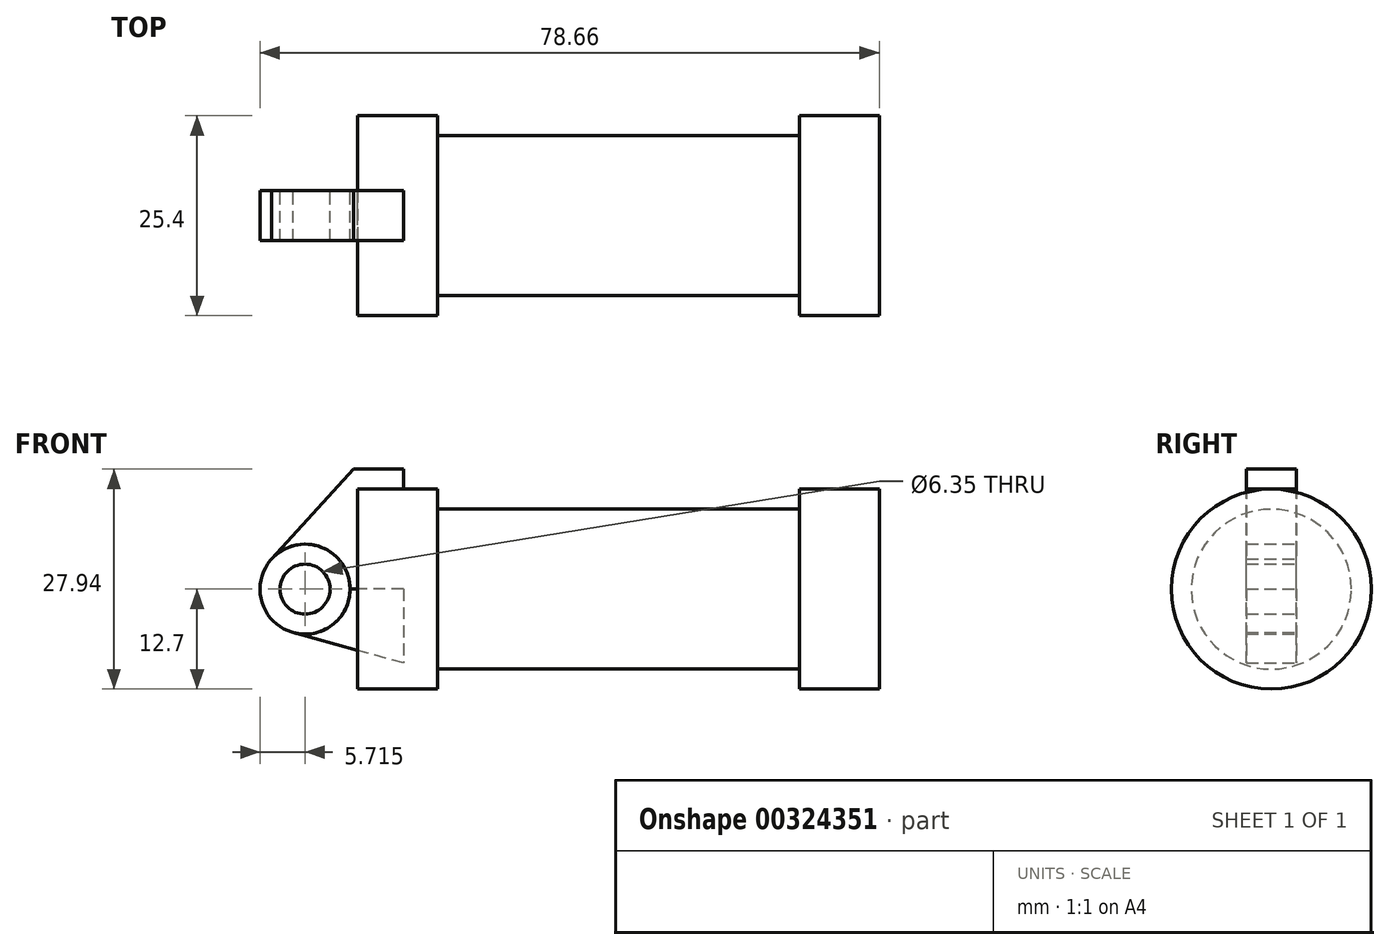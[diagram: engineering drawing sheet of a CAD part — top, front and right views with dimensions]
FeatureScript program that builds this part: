
annotation { "Feature Type Name" : "Feature", "Feature Type Description" : "" }
export const myFeature = defineFeature(function(context is Context, id is Id, definition is map)
    precondition{}
    {
        {
            var Q0;
            Q0=qCreatedBy(makeId("Front.planeOp"),FACE);
            var sketch = newSketch(context, id + "F0", { "sketchPlane" : qUnion([Q0])});
            skLineSegment(sketch, "E0", {"start": v(0, 0) * mm, "end": v(0, 12.7) * mm});
            skLineSegment(sketch, "E1", {"start": v(0, 12.7) * mm, "end": v(10.16, 12.7) * mm});
            skLineSegment(sketch, "E2", {"start": v(10.16, 12.7) * mm, "end": v(10.16, 10.16) * mm});
            skLineSegment(sketch, "E3", {"start": v(10.16, 10.16) * mm, "end": v(56.13, 10.16) * mm});
            skLineSegment(sketch, "E4", {"start": v(56.13, 10.16) * mm, "end": v(56.13, 12.7) * mm});
            skLineSegment(sketch, "E5", {"start": v(56.13, 12.7) * mm, "end": v(66.3, 12.7) * mm});
            skLineSegment(sketch, "E6", {"start": v(66.3, 12.7) * mm, "end": v(66.3, 0) * mm});
            skLineSegment(sketch, "E7", {"start": v(66.3, 0) * mm, "end": v(0, 0) * mm});
            skLineSegment(sketch, "E8", {"start": v(5.84, 15.24) * mm, "end": v(-0.5, 15.24) * mm});
            skLineSegment(sketch, "E9", {"start": v(-0.5, 15.24) * mm, "end": v(-10.88, 3.85) * mm});
            skLineSegment(sketch, "E10", {"start": v(0, 0) * mm, "end": v(-6.65, 0) * mm});
            skCircle(sketch, "E11", {"center": v(-6.65, 0) * mm, "radius": 5.72 * mm});
            skCircle(sketch, "E12", {"center": v(-6.65, 0) * mm, "radius": 3.18 * mm});
            skLineSegment(sketch, "E13", {"start": v(5.84, 15.24) * mm, "end": v(5.84, -9.4) * mm});
            skLineSegment(sketch, "E14", {"start": v(5.84, -9.4) * mm, "end": v(-8.18, -5.5) * mm});
            skSolve(sketch);
        }
        {
            var Q0;
            {var subQ0=sQuery(id+"F0.wireOp",EDGE,"E2");Q0=makeQuery(id+"F0.imprint","IMPRINT",FACE,{"disambiguationData":[TD([[makeQuery(id+"F0.imprint","IMPRINT",EDGE,{"derivedFrom":subQ0}),-1.0]])]});}
            var Q1;
            {var subQ0=sQuery(id+"F0.wireOp",EDGE,"E0");Q1=makeQuery(id+"F0.imprint","IMPRINT",FACE,{"disambiguationData":[TD([[makeQuery(id+"F0.imprint","IMPRINT",EDGE,{"derivedFrom":subQ0}),-1.0]])]});}
            var Q2;
            Q2=sQuery(id+"F0.wireOp",EDGE,"E10");
            revolve(context, id + "F1", {"entities" : qUnion([Q0, Q1]), "axis" : qUnion([Q2]), "revolveType" : RevolveType.FULL});
        }
        {
            var Q0;
            {var subQ5=sQuery(id+"F0.wireOp",EDGE,"E12");Q0=makeQuery(id+"F0.imprint","IMPRINT",FACE,{"disambiguationData":[TD([[makeQuery(id+"F0.imprint","IMPRINT",EDGE,{"derivedFrom":subQ5}),-1.0]])]});}
            extrude(context, id + "F2", {"entities" : qUnion([Q0]), "operationType" : NewBodyOperationType.ADD, "endBound" : BoundingType.SYMMETRIC, "depth" : 6.35 * mm});
        }
        {
            var Q0;
            {var subQ1=sQuery(id+"F0.wireOp",EDGE,"E0");Q0=makeQuery(id+"F0.imprint","IMPRINT",FACE,{"disambiguationData":[TD([[makeQuery(id+"F0.imprint","IMPRINT",EDGE,{"derivedFrom":subQ1}),1.0]])]});}
            extrude(context, id + "F3", {"entities" : qUnion([Q0]), "endBound" : BoundingType.SYMMETRIC, "depth" : 6.35 * mm});
        }
        {
            var Q0;
            {var subQ0=sQuery(id+"F0.wireOp",EDGE,"E14");Q0=makeQuery(id+"F0.imprint","IMPRINT",FACE,{"disambiguationData":[TD([[makeQuery(id+"F0.imprint","IMPRINT",EDGE,{"derivedFrom":subQ0}),-1.0]])]});}
            extrude(context, id + "F4", {"entities" : qUnion([Q0]), "endBound" : BoundingType.SYMMETRIC, "depth" : 6.35 * mm});
        }
    });
